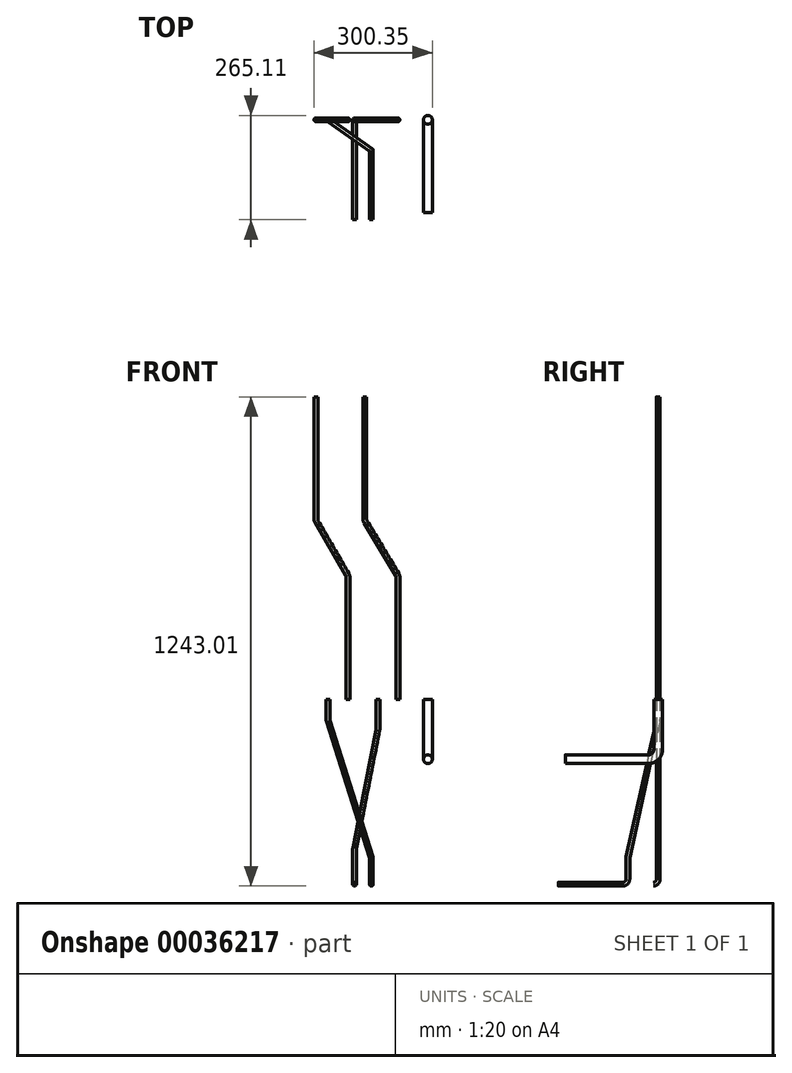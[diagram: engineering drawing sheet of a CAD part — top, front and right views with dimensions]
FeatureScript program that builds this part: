
annotation { "Feature Type Name" : "Feature", "Feature Type Description" : "" }
export const myFeature = defineFeature(function(context is Context, id is Id, definition is map)
    precondition{}
    {
        {
            var Q0;
            Q0=qCreatedBy(makeId("Top.planeOp"),FACE);
            var sketch = newSketch(context, id + "F0", { "sketchPlane" : qUnion([Q0])});
            skCircle(sketch, "E0", {"center": v(0, 0) * mm, "radius": 4.76 * mm});
            skCircle(sketch, "E1", {"center": v(-127, 0) * mm, "radius": 4.76 * mm});
            skCircle(sketch, "E2", {"center": v(-50.8, 0) * mm, "radius": 4.76 * mm});
            skCircle(sketch, "E3", {"center": v(-177.8, 0) * mm, "radius": 4.76 * mm});
            skCircle(sketch, "E4", {"center": v(76.2, 0) * mm, "radius": 11.11 * mm});
            skLineSegment(sketch, "E5", {"start": v(-177.8, 0) * mm, "end": v(-146.6, -21.85) * mm, "construction": true});
            skLineSegment(sketch, "E6", {"start": v(-177.8, 0) * mm, "end": v(-139.7, 0) * mm, "construction": true});
            skSolve(sketch);
        }
        {
            var Q0;
            Q0=qCreatedBy(makeId("Front.planeOp"),FACE);
            var sketch = newSketch(context, id + "F1", { "sketchPlane" : qUnion([Q0])});
            skLineSegment(sketch, "E7", {"start": v(0, 0) * mm, "end": v(0, 310.8) * mm});
            skLineSegment(sketch, "E8", {"start": v(-1.82, 317.35) * mm, "end": v(-82.26, 451) * mm});
            skLineSegment(sketch, "E9", {"start": v(-84.07, 457.55) * mm, "end": v(-84.07, 768.35) * mm});
            skPoint(sketch, "E10.visualSharp", {"position": v(-84.07, 454.03) * mm});
            skArc(sketch, "E10.filletArc", {"start": v(-84.07, 457.55) * mm, "mid": v(-83.61, 454.15) * mm, "end": v(-82.26, 451) * mm});
            skPoint(sketch, "E11.visualSharp", {"position": v(0, 314.33) * mm});
            skArc(sketch, "E11.filletArc", {"start": v(0, 310.8) * mm, "mid": v(-0.46, 314.2) * mm, "end": v(-1.82, 317.35) * mm});
            skLineSegment(sketch, "E12", {"start": v(-127, 0) * mm, "end": v(-127, 310.8) * mm});
            skLineSegment(sketch, "E13", {"start": v(-128.72, 317.18) * mm, "end": v(-206.56, 451.17) * mm});
            skLineSegment(sketch, "E14", {"start": v(-208.28, 457.55) * mm, "end": v(-208.28, 768.35) * mm});
            skPoint(sketch, "E15.visualSharp", {"position": v(-208.28, 454.13) * mm});
            skArc(sketch, "E15.filletArc", {"start": v(-208.28, 457.55) * mm, "mid": v(-207.84, 454.25) * mm, "end": v(-206.56, 451.17) * mm});
            skPoint(sketch, "E16.visualSharp", {"position": v(-127, 314.22) * mm});
            skArc(sketch, "E16.filletArc", {"start": v(-127, 310.8) * mm, "mid": v(-127.44, 314.1) * mm, "end": v(-128.72, 317.18) * mm});
            skLineSegment(sketch, "E17", {"start": v(-50.8, 0) * mm, "end": v(-50.8, -76.2) * mm});
            skLineSegment(sketch, "E18", {"start": v(-51.04, -78.65) * mm, "end": v(-110, -378.55) * mm});
            skLineSegment(sketch, "E19", {"start": v(-110.24, -381) * mm, "end": v(-110.24, -457.2) * mm});
            skPoint(sketch, "E20.visualSharp", {"position": v(-110.24, -379.76) * mm});
            skArc(sketch, "E20.filletArc", {"start": v(-110, -378.55) * mm, "mid": v(-110.18, -379.77) * mm, "end": v(-110.24, -381) * mm});
            skPoint(sketch, "E21.visualSharp", {"position": v(-50.8, -77.44) * mm});
            skArc(sketch, "E21.filletArc", {"start": v(-51.04, -78.65) * mm, "mid": v(-50.86, -77.43) * mm, "end": v(-50.8, -76.2) * mm});
            skSolve(sketch);
        }
        {
            var Q0;
            Q0=makeQuery(id+"F0.imprint","IMPRINT",FACE,{"disambiguationData":[TD([[makeQuery(id+"F0.imprint","IMPRINT",EDGE,{"derivedFrom":sQuery(id+"F0.wireOp",EDGE,"E0")}),1.0]])]});
            var Q1;
            Q1=sQuery(id+"F1.wireOp",EDGE,"E7");
            var Q2;
            Q2=sQuery(id+"F1.wireOp",EDGE,"E11.filletArc");
            var Q3;
            Q3=sQuery(id+"F1.wireOp",EDGE,"E8");
            var Q4;
            Q4=sQuery(id+"F1.wireOp",EDGE,"E10.filletArc");
            var Q5;
            Q5=sQuery(id+"F1.wireOp",EDGE,"E9");
            sweep(context, id + "F2", {"profiles" : qUnion([Q0]), "path" : qUnion([Q1, Q2, Q3, Q4, Q5])});
        }
        {
            var Q0;
            Q0=makeQuery(id+"F0.imprint","IMPRINT",FACE,{"disambiguationData":[TD([[makeQuery(id+"F0.imprint","IMPRINT",EDGE,{"derivedFrom":sQuery(id+"F0.wireOp",EDGE,"E1")}),1.0]])]});
            var Q1;
            Q1=sQuery(id+"F1.wireOp",EDGE,"E12");
            var Q2;
            Q2=sQuery(id+"F1.wireOp",EDGE,"E16.filletArc");
            var Q3;
            Q3=sQuery(id+"F1.wireOp",EDGE,"E13");
            var Q4;
            Q4=sQuery(id+"F1.wireOp",EDGE,"E15.filletArc");
            var Q5;
            Q5=sQuery(id+"F1.wireOp",EDGE,"E14");
            sweep(context, id + "F3", {"profiles" : qUnion([Q0]), "path" : qUnion([Q1, Q2, Q3, Q4, Q5])});
        }
        {
            var Q0;
            Q0=qCreatedBy(makeId("Right.planeOp"),FACE);
            var Q1;
            Q1=sQuery(id+"F1.wireOp",VERTEX,"E19.end");
            cPlane(context, id + "F4", {"entities" : qUnion([Q0, Q1]), "cplaneType" : CPlaneType.PLANE_POINT, "offset" : 152.4 * mm, "width" : 152.4 * mm, "height" : 152.4 * mm});
        }
        {
            var Q0;
            Q0=qCreatedBy(makeId("Right.planeOp"),FACE);
            var Q1;
            Q1=sQuery(id+"F0.wireOp",VERTEX,"E4.center");
            cPlane(context, id + "F5", {"entities" : qUnion([Q0, Q1]), "cplaneType" : CPlaneType.PLANE_POINT, "offset" : 152.4 * mm, "width" : 152.4 * mm, "height" : 152.4 * mm});
        }
        {
            var Q0;
            Q0=qCreatedBy(id+"F5.planeOp",FACE);
            var sketch = newSketch(context, id + "F6", { "sketchPlane" : qUnion([Q0])});
            skLineSegment(sketch, "E22", {"start": v(0, 0) * mm, "end": v(0, -127) * mm});
            skLineSegment(sketch, "E23", {"start": v(-25.4, -152.4) * mm, "end": v(-236.22, -152.4) * mm});
            skPoint(sketch, "E24.visualSharp", {"position": v(0, -152.4) * mm});
            skArc(sketch, "E24.filletArc", {"start": v(-25.4, -152.4) * mm, "mid": v(-7.44, -144.96) * mm, "end": v(0, -127) * mm});
            skSolve(sketch);
        }
        {
            var Q0;
            Q0=makeQuery(id+"F0.imprint","IMPRINT",FACE,{"disambiguationData":[TD([[makeQuery(id+"F0.imprint","IMPRINT",EDGE,{"derivedFrom":sQuery(id+"F0.wireOp",EDGE,"E4")}),1.0]])]});
            var Q1;
            Q1=makeQuery(id+"F0.imprint","IMPRINT",FACE,{"disambiguationData":[TD([[makeQuery(id+"F0.imprint","IMPRINT",EDGE,{"derivedFrom":sQuery(id+"F0.wireOp",EDGE,"13a35655-1456-4fea-a458-14109ce3cf0a")}),1.0]])]});
            var Q2;
            Q2=sQuery(id+"F6.wireOp",EDGE,"E22");
            var Q3;
            Q3=sQuery(id+"F6.wireOp",EDGE,"E24.filletArc");
            var Q4;
            Q4=sQuery(id+"F6.wireOp",EDGE,"E23");
            sweep(context, id + "F7", {"profiles" : qUnion([Q0, Q1]), "path" : qUnion([Q2, Q3, Q4])});
        }
        {
            var Q0;
            Q0=qCreatedBy(id+"F4.planeOp",FACE);
            var sketch = newSketch(context, id + "F8", { "sketchPlane" : qUnion([Q0])});
            skArc(sketch, "E25", {"start": v(-12.7, -469.9) * mm, "mid": v(-3.72, -466.18) * mm, "end": v(0, -457.2) * mm});
            skLineSegment(sketch, "E26", {"start": v(-12.7, -469.9) * mm, "end": v(-254, -469.9) * mm});
            skSolve(sketch);
        }
        {
            var Q0;
            Q0=makeQuery(id+"F0.imprint","IMPRINT",FACE,{"disambiguationData":[TD([[makeQuery(id+"F0.imprint","IMPRINT",EDGE,{"derivedFrom":sQuery(id+"F0.wireOp",EDGE,"E2")}),1.0]])]});
            var Q1;
            Q1=sQuery(id+"F1.wireOp",EDGE,"E17");
            var Q2;
            Q2=sQuery(id+"F1.wireOp",EDGE,"E21.filletArc");
            var Q3;
            Q3=sQuery(id+"F1.wireOp",EDGE,"E18");
            var Q4;
            Q4=sQuery(id+"F1.wireOp",EDGE,"E20.filletArc");
            var Q5;
            Q5=sQuery(id+"F1.wireOp",EDGE,"E19");
            var Q6;
            Q6=sQuery(id+"F8.wireOp",EDGE,"E25");
            var Q7;
            Q7=sQuery(id+"F8.wireOp",EDGE,"E26");
            sweep(context, id + "F9", {"profiles" : qUnion([Q0]), "path" : qUnion([Q1, Q2, Q3, Q4, Q5, Q6, Q7])});
        }
        {
            var Q0;
            Q0=qCreatedBy(makeId("Front.planeOp"),FACE);
            var Q1;
            Q1=sQuery(id+"F0.wireOp",EDGE,"E5");
            cPlane(context, id + "F10", {"entities" : qUnion([Q0, Q1]), "cplaneType" : CPlaneType.LINE_ANGLE, "offset" : 152.4 * mm, "angle" : 0 * degree, "width" : 152.4 * mm, "height" : 152.4 * mm});
        }
        {
            var Q0;
            Q0=qCreatedBy(id+"F10.planeOp",FACE);
            var sketch = newSketch(context, id + "F11", { "sketchPlane" : qUnion([Q0])});
            skLineSegment(sketch, "E27", {"start": v(145.65, 0) * mm, "end": v(145.65, -50.8) * mm});
            skLineSegment(sketch, "E28", {"start": v(144.8, -55.35) * mm, "end": v(11.87, -401.85) * mm});
            skLineSegment(sketch, "E29", {"start": v(11.03, -406.4) * mm, "end": v(11.03, -457.2) * mm});
            skPoint(sketch, "E30.visualSharp", {"position": v(145.65, -53.15) * mm});
            skArc(sketch, "E30.filletArc", {"start": v(144.8, -55.35) * mm, "mid": v(145.43, -53.11) * mm, "end": v(145.65, -50.8) * mm});
            skPoint(sketch, "E31.visualSharp", {"position": v(11.03, -404.05) * mm});
            skArc(sketch, "E31.filletArc", {"start": v(11.87, -401.85) * mm, "mid": v(11.24, -404.09) * mm, "end": v(11.03, -406.4) * mm});
            skSolve(sketch);
        }
        {
            var Q0;
            Q0=qCreatedBy(makeId("Right.planeOp"),FACE);
            var Q1;
            Q1=sQuery(id+"F11.wireOp",VERTEX,"E29.end");
            cPlane(context, id + "F12", {"entities" : qUnion([Q0, Q1]), "cplaneType" : CPlaneType.PLANE_POINT, "offset" : 152.4 * mm, "width" : 152.4 * mm, "height" : 152.4 * mm});
        }
        {
            var Q0;
            Q0=qCreatedBy(id+"F12.planeOp",FACE);
            var sketch = newSketch(context, id + "F13", { "sketchPlane" : qUnion([Q0])});
            skArc(sketch, "E32", {"start": v(-89.91, -469.9) * mm, "mid": v(-80.93, -466.18) * mm, "end": v(-77.21, -457.2) * mm});
            skLineSegment(sketch, "E33", {"start": v(-89.91, -469.9) * mm, "end": v(-254, -469.9) * mm});
            skSolve(sketch);
        }
        {
            var Q0;
            Q0=makeQuery(id+"F0.imprint","IMPRINT",FACE,{"disambiguationData":[TD([[makeQuery(id+"F0.imprint","IMPRINT",EDGE,{"derivedFrom":sQuery(id+"F0.wireOp",EDGE,"E3")}),1.0]])]});
            var Q1;
            Q1=sQuery(id+"F11.wireOp",EDGE,"E27");
            var Q2;
            Q2=sQuery(id+"F11.wireOp",EDGE,"E30.filletArc");
            var Q3;
            Q3=sQuery(id+"F11.wireOp",EDGE,"E28");
            var Q4;
            Q4=sQuery(id+"F11.wireOp",EDGE,"E31.filletArc");
            var Q5;
            Q5=sQuery(id+"F11.wireOp",EDGE,"E29");
            var Q6;
            Q6=sQuery(id+"F13.wireOp",EDGE,"E32");
            var Q7;
            Q7=sQuery(id+"F13.wireOp",EDGE,"E33");
            sweep(context, id + "F14", {"profiles" : qUnion([Q0]), "path" : qUnion([Q1, Q2, Q3, Q4, Q5, Q6, Q7])});
        }
    });
